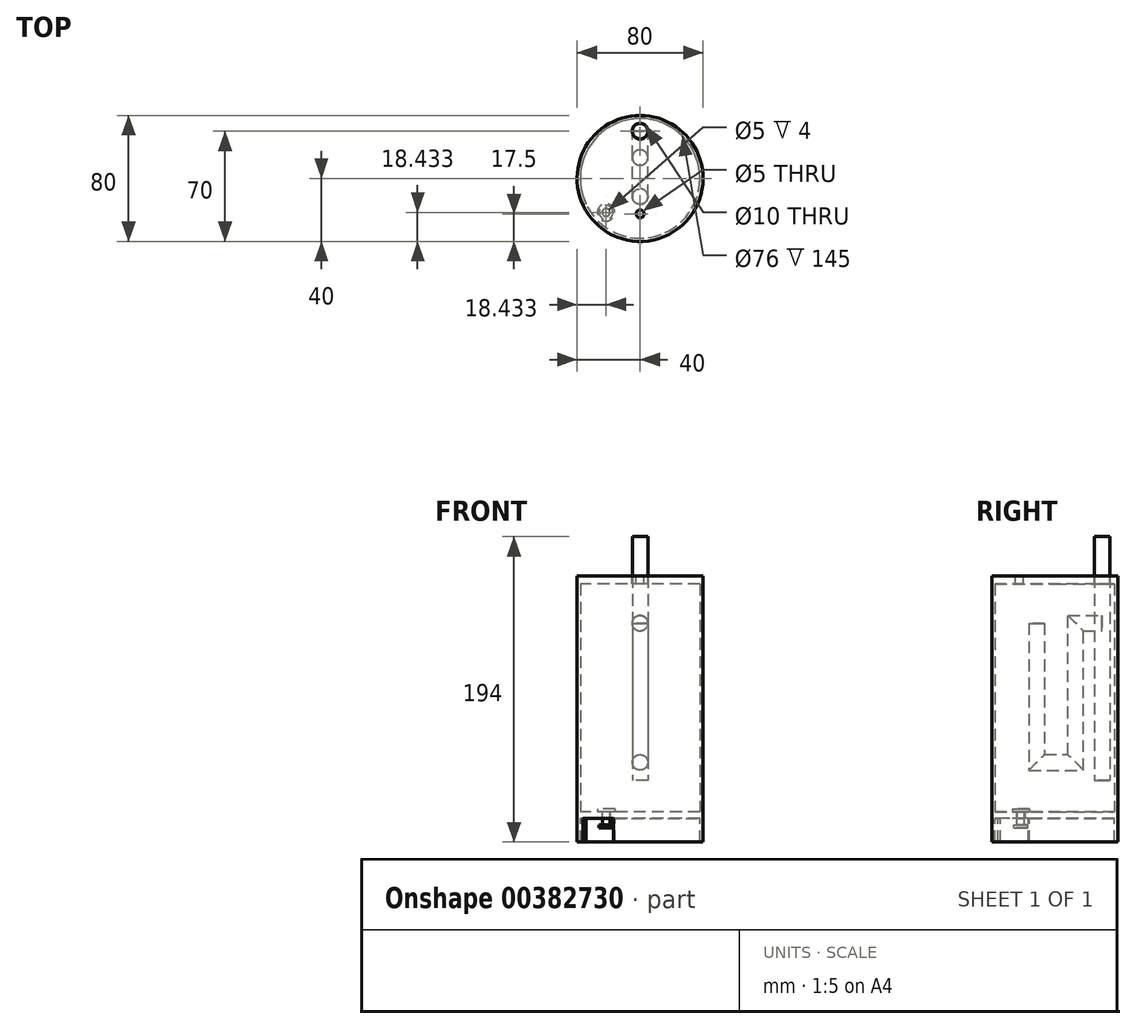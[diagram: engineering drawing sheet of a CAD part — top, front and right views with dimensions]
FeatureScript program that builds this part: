
annotation { "Feature Type Name" : "Feature", "Feature Type Description" : "" }
export const myFeature = defineFeature(function(context is Context, id is Id, definition is map)
    precondition{}
    {
        {
            var Q0;
            Q0=qCreatedBy(makeId("Top.planeOp"),FACE);
            var sketch = newSketch(context, id + "F0", { "sketchPlane" : qUnion([Q0])});
            skCircle(sketch, "E0", {"center": v(0, 0) * mm, "radius": 40 * mm});
            skCircle(sketch, "E1.0", {"center": v(0, 0) * mm, "radius": 38 * mm});
            skSolve(sketch);
        }
        {
            var Q0;
            Q0=makeQuery(id+"F0.imprint","IMPRINT",FACE,{"disambiguationData":[TD([[makeQuery(id+"F0.imprint","IMPRINT",EDGE,{"derivedFrom":sQuery(id+"F0.wireOp",EDGE,"E0")}),1.0]])]});
            extrude(context, id + "F1", {"entities" : qUnion([Q0]), "depth" : 150 * mm});
        }
        {
            var Q0;
            Q0=makeQuery(id+"F1.opExtrude","CAP_FACE",FACE,{"disambiguationData":[OSD([sQuery(id+"F0.wireOp",EDGE,"E0"),sQuery(id+"F0.wireOp",EDGE,"E1.0")])],"isStart":false});
            var sketch = newSketch(context, id + "F2", { "sketchPlane" : qUnion([Q0])});
            skCircle(sketch, "E2.0", {"center": v(0, 0) * mm, "radius": 38 * mm});
            skCircle(sketch, "E3.0", {"center": v(0, 0) * mm, "radius": 40 * mm});
            skSolve(sketch);
        }
        {
            var Q0;
            Q0=makeQuery(id+"F2.imprint","IMPRINT",FACE,{"disambiguationData":[TD([[makeQuery(id+"F2.imprint","IMPRINT",EDGE,{"derivedFrom":sQuery(id+"F2.wireOp",EDGE,"E2.0")}),1.0]])]});
            extrude(context, id + "F3", {"entities" : qUnion([Q0]), "oppositeDirection" : true, "depth" : 3 * mm});
        }
        {
            var Q0;
            Q0=makeQuery(id+"F2.imprint","IMPRINT",FACE,{"disambiguationData":[TD([[makeQuery(id+"F2.imprint","IMPRINT",EDGE,{"derivedFrom":sQuery(id+"F2.wireOp",EDGE,"E2.0")}),-1.0]])]});
            var Q1;
            Q1=makeQuery(id+"F2.imprint","IMPRINT",FACE,{"disambiguationData":[TD([[makeQuery(id+"F2.imprint","IMPRINT",EDGE,{"derivedFrom":sQuery(id+"F2.wireOp",EDGE,"E2.0")}),1.0]])]});
            extrude(context, id + "F4", {"entities" : qUnion([Q0, Q1]), "operationType" : NewBodyOperationType.ADD, "depth" : 2 * mm});
        }
        {
            var Q0;
            Q0=makeQuery(id+"F0.imprint","IMPRINT",FACE,{"disambiguationData":[TD([[makeQuery(id+"F0.imprint","IMPRINT",EDGE,{"derivedFrom":sQuery(id+"F0.wireOp",EDGE,"E1.0")}),1.0]])]});
            extrude(context, id + "F5", {"entities" : qUnion([Q0]), "depth" : 2 * mm});
        }
        {
            var Q0;
            Q0=makeQuery(id+"F0.imprint","IMPRINT",FACE,{"disambiguationData":[TD([[makeQuery(id+"F0.imprint","IMPRINT",EDGE,{"derivedFrom":sQuery(id+"F0.wireOp",EDGE,"E0")}),1.0]])]});
            var Q1;
            Q1=makeQuery(id+"F0.imprint","IMPRINT",FACE,{"disambiguationData":[TD([[makeQuery(id+"F0.imprint","IMPRINT",EDGE,{"derivedFrom":sQuery(id+"F0.wireOp",EDGE,"E1.0")}),1.0]])]});
            extrude(context, id + "F6", {"entities" : qUnion([Q0, Q1]), "operationType" : NewBodyOperationType.ADD, "oppositeDirection" : true, "depth" : 2 * mm});
        }
        {
            var Q0;
            Q0=makeQuery(id+"F6.opExtrude","CAP_FACE",FACE,{"disambiguationData":[OSD([sQuery(id+"F0.wireOp",EDGE,"E0")])],"isStart":false});
            var sketch = newSketch(context, id + "F7", { "sketchPlane" : qUnion([Q0])});
            skCircle(sketch, "E4.0", {"center": v(0, 0) * mm, "radius": 40 * mm});
            skCircle(sketch, "E5.0", {"center": v(0, 0) * mm, "radius": 38 * mm});
            skLineSegment(sketch, "E6", {"start": v(0, 0) * mm, "end": v(-36.25, 16.9) * mm});
            skLineSegment(sketch, "E7", {"start": v(0, 0) * mm, "end": v(-16.9, 36.25) * mm});
            skLineSegment(sketch, "E8", {"start": v(0, 0) * mm, "end": v(-28.28, 28.28) * mm, "construction": true});
            skCircle(sketch, "E9", {"center": v(-21.57, 21.57) * mm, "radius": 2.5 * mm});
            skSolve(sketch);
        }
        {
            var Q0;
            {var subQ0=sQuery(id+"F7.wireOp",EDGE,"E6");var subQ1=sQuery(id+"F7.wireOp",EDGE,"E4.0");var subQ2=makeQuery(id+"F7.imprint","INTERSECT",VERTEX,{"derivedFrom":[subQ1,subQ0]});Q0=makeQuery(id+"F7.imprint","IMPRINT",FACE,{"disambiguationData":[TD([[makeQuery(id+"F7.imprint","IMPRINT",EDGE,{"disambiguationData":[TD([[subQ2,1.0]])],"derivedFrom":subQ1}),-1.0]])]});}
            extrude(context, id + "F8", {"entities" : qUnion([Q0]), "operationType" : NewBodyOperationType.ADD, "depth" : 15 * mm});
        }
        {
            var Q0;
            Q0=makeQuery(id+"F7.imprint","IMPRINT",FACE,{"disambiguationData":[TD([[makeQuery(id+"F7.imprint","IMPRINT",EDGE,{"derivedFrom":sQuery(id+"F7.wireOp",EDGE,"E9")}),1.0]])]});
            extrude(context, id + "F9", {"entities" : qUnion([Q0]), "operationType" : NewBodyOperationType.REMOVE, "endBound" : BoundingType.UP_TO_NEXT, "oppositeDirection" : true, "depth" : 25 * mm});
        }
        {
            var Q0;
            Q0=makeQuery(id+"F5.opExtrude","CAP_FACE",FACE,{"disambiguationData":[OSD([sQuery(id+"F0.wireOp",EDGE,"E1.0")])],"isStart":false});
            var sketch = newSketch(context, id + "F10", { "sketchPlane" : qUnion([Q0])});
            skCircle(sketch, "E10.0", {"center": v(-21.57, -21.57) * mm, "radius": 2.5 * mm});
            skCircle(sketch, "E11.0", {"center": v(-21.57, -21.57) * mm, "radius": 2.4 * mm});
            skCircle(sketch, "E12.0", {"center": v(-21.57, -21.57) * mm, "radius": 5.5 * mm});
            skCircle(sketch, "E13.0", {"center": v(0, 0) * mm, "radius": 43 * mm});
            skSolve(sketch);
        }
        {
            var Q0;
            Q0=makeQuery(id+"F10.imprint","IMPRINT",FACE,{"disambiguationData":[TD([[makeQuery(id+"F10.imprint","IMPRINT",EDGE,{"derivedFrom":sQuery(id+"F10.wireOp",EDGE,"E11.0")}),1.0]])]});
            extrude(context, id + "F11", {"entities" : qUnion([Q0]), "oppositeDirection" : true, "depth" : 8 * mm});
        }
        {
            var Q0;
            Q0=makeQuery(id+"F10.imprint","IMPRINT",FACE,{"disambiguationData":[TD([[makeQuery(id+"F10.imprint","IMPRINT",EDGE,{"derivedFrom":sQuery(id+"F10.wireOp",EDGE,"E10.0")}),1.0]])]});
            var Q1;
            Q1=makeQuery(id+"F10.imprint","IMPRINT",FACE,{"disambiguationData":[TD([[makeQuery(id+"F10.imprint","IMPRINT",EDGE,{"derivedFrom":sQuery(id+"F10.wireOp",EDGE,"E10.0")}),-1.0]])]});
            var Q2;
            Q2=makeQuery(id+"F10.imprint","IMPRINT",FACE,{"disambiguationData":[TD([[makeQuery(id+"F10.imprint","IMPRINT",EDGE,{"derivedFrom":sQuery(id+"F10.wireOp",EDGE,"E11.0")}),1.0]])]});
            extrude(context, id + "F12", {"entities" : qUnion([Q0, Q1, Q2]), "operationType" : NewBodyOperationType.ADD, "depth" : 2 * mm});
        }
        {
            var Q0;
            Q0=makeQuery(id+"F11.opExtrude","CAP_FACE",FACE,{"disambiguationData":[OSD([sQuery(id+"F10.wireOp",EDGE,"E11.0")])],"isStart":false});
            var sketch = newSketch(context, id + "F13", { "sketchPlane" : qUnion([Q0])});
            skCircle(sketch, "E14.0", {"center": v(-21.57, 21.57) * mm, "radius": 2.4 * mm});
            skCircle(sketch, "E15.0", {"center": v(-21.57, 21.57) * mm, "radius": 4.4 * mm});
            skSolve(sketch);
        }
        {
            var Q0;
            Q0=makeQuery(id+"F13.imprint","IMPRINT",FACE,{"disambiguationData":[TD([[makeQuery(id+"F13.imprint","IMPRINT",EDGE,{"derivedFrom":sQuery(id+"F13.wireOp",EDGE,"E14.0")}),1.0]])]});
            var Q1;
            Q1=makeQuery(id+"F13.imprint","IMPRINT",FACE,{"disambiguationData":[TD([[makeQuery(id+"F13.imprint","IMPRINT",EDGE,{"derivedFrom":sQuery(id+"F13.wireOp",EDGE,"E14.0")}),-1.0]])]});
            extrude(context, id + "F14", {"entities" : qUnion([Q0, Q1]), "depth" : 2 * mm});
        }
        {
            var Q0;
            Q0=makeQuery(id+"F4.opExtrude","CAP_FACE",FACE,{"disambiguationData":[OSD([sQuery(id+"F2.wireOp",EDGE,"E3.0")])],"isStart":false});
            var sketch = newSketch(context, id + "F15", { "sketchPlane" : qUnion([Q0])});
            skCircle(sketch, "E16.0", {"center": v(0, 0) * mm, "radius": 40 * mm});
            skLineSegment(sketch, "E17", {"start": v(0, 0) * mm, "end": v(0, 40) * mm, "construction": true});
            skCircle(sketch, "E18", {"center": v(0, 30) * mm, "radius": 4 * mm});
            skCircle(sketch, "E19.0", {"center": v(0, 30) * mm, "radius": 5 * mm});
            skLineSegment(sketch, "E20", {"start": v(0, 0) * mm, "end": v(0, -40) * mm, "construction": true});
            skCircle(sketch, "E21", {"center": v(0, -22.5) * mm, "radius": 2.5 * mm});
            skCircle(sketch, "E22.0", {"center": v(0, -22.5) * mm, "radius": 2 * mm});
            skLineSegment(sketch, "E23.0", {"start": v(-5, 0) * mm, "end": v(-5, -40) * mm});
            skSolve(sketch);
        }
        {
            var Q0;
            Q0=makeQuery(id+"F15.imprint","IMPRINT",FACE,{"disambiguationData":[TD([[makeQuery(id+"F15.imprint","IMPRINT",EDGE,{"derivedFrom":sQuery(id+"F15.wireOp",EDGE,"E18")}),-1.0]])]});
            var Q1;
            Q1=makeQuery(id+"F15.imprint","IMPRINT",FACE,{"disambiguationData":[TD([[makeQuery(id+"F15.imprint","IMPRINT",EDGE,{"derivedFrom":sQuery(id+"F15.wireOp",EDGE,"E18")}),1.0]])]});
            var Q2;
            Q2=makeQuery(id+"F15.imprint","IMPRINT",FACE,{"disambiguationData":[TD([[makeQuery(id+"F15.imprint","IMPRINT",EDGE,{"derivedFrom":sQuery(id+"F15.wireOp",EDGE,"E22.0")}),1.0]])]});
            var Q3;
            Q3=makeQuery(id+"F15.imprint","IMPRINT",FACE,{"disambiguationData":[TD([[makeQuery(id+"F15.imprint","IMPRINT",EDGE,{"derivedFrom":sQuery(id+"F15.wireOp",EDGE,"E21")}),1.0]])]});
            extrude(context, id + "F16", {"entities" : qUnion([Q0, Q1, Q2, Q3]), "operationType" : NewBodyOperationType.REMOVE, "endBound" : BoundingType.UP_TO_NEXT, "oppositeDirection" : true, "depth" : 25 * mm});
        }
        {
            var Q0;
            Q0=makeQuery(id+"F4.opExtrude","CAP_FACE",FACE,{"disambiguationData":[OSD([sQuery(id+"F2.wireOp",EDGE,"E3.0")])],"isStart":false});
            var sketch = newSketch(context, id + "F17", { "sketchPlane" : qUnion([Q0])});
            skCircle(sketch, "E24.0", {"center": v(0, 30) * mm, "radius": 5 * mm});
            skCircle(sketch, "E25.0", {"center": v(0, 30) * mm, "radius": 4.9 * mm});
            skSolve(sketch);
        }
        {
            var Q0;
            Q0=makeQuery(id+"F17.imprint","IMPRINT",FACE,{"disambiguationData":[TD([[makeQuery(id+"F17.imprint","IMPRINT",EDGE,{"derivedFrom":sQuery(id+"F17.wireOp",EDGE,"E25.0")}),1.0]])]});
            extrude(context, id + "F18", {"entities" : qUnion([Q0]), "depth" : 25 * mm, "hasSecondDirection" : true, "secondDirectionOppositeDirection" : true, "secondDirectionDepth" : 130 * mm});
        }
        {
            var Q0;
            Q0=qCreatedBy(makeId("Right.planeOp"),FACE);
            var sketch = newSketch(context, id + "F19", { "sketchPlane" : qUnion([Q0])});
            skLineSegment(sketch, "E26", {"start": v(30, 152) * mm, "end": v(30, 17) * mm});
            skLineSegment(sketch, "E27", {"start": v(30, 152) * mm, "end": v(30, 203.38) * mm});
            skLineSegment(sketch, "E28", {"start": v(30, 122) * mm, "end": v(13.27, 122) * mm});
            skLineSegment(sketch, "E29", {"start": v(13.27, 122) * mm, "end": v(13.27, 33.6) * mm});
            skLineSegment(sketch, "E30", {"start": v(13.27, 33.6) * mm, "end": v(-11.51, 33.6) * mm});
            skLineSegment(sketch, "E31", {"start": v(-11.51, 33.6) * mm, "end": v(-11.51, 122) * mm});
            skSolve(sketch);
        }
        {
            var Q0;
            Q0=sQuery(id+"F19.wireOp",VERTEX,"E31.end");
            var Q1;
            Q1=sQuery(id+"F19.wireOp",EDGE,"E31");
            cPlane(context, id + "F20", {"entities" : qUnion([Q0, Q1]), "cplaneType" : CPlaneType.CURVE_POINT, "offset" : 25 * mm, "width" : 150 * mm, "height" : 150 * mm});
        }
        {
            var Q0;
            Q0=qCreatedBy(id+"F20.planeOp",FACE);
            var sketch = newSketch(context, id + "F21", { "sketchPlane" : qUnion([Q0])});
            skCircle(sketch, "E32", {"center": v(0, -11.51) * mm, "radius": 4.95 * mm});
            skSolve(sketch);
        }
        {
            var Q0;
            Q0=makeQuery(id+"F21.imprint","IMPRINT",FACE,{"disambiguationData":[TD([[makeQuery(id+"F21.imprint","IMPRINT",EDGE,{"derivedFrom":sQuery(id+"F21.wireOp",EDGE,"E32")}),1.0]])]});
            var Q1;
            Q1=sQuery(id+"F19.wireOp",EDGE,"E31");
            var Q2;
            Q2=sQuery(id+"F19.wireOp",EDGE,"E30");
            var Q3;
            Q3=sQuery(id+"F19.wireOp",EDGE,"E29");
            var Q4;
            Q4=sQuery(id+"F19.wireOp",EDGE,"E28");
            sweep(context, id + "F22", {"profiles" : qUnion([Q0]), "path" : qUnion([Q1, Q2, Q3, Q4])});
        }
    });
